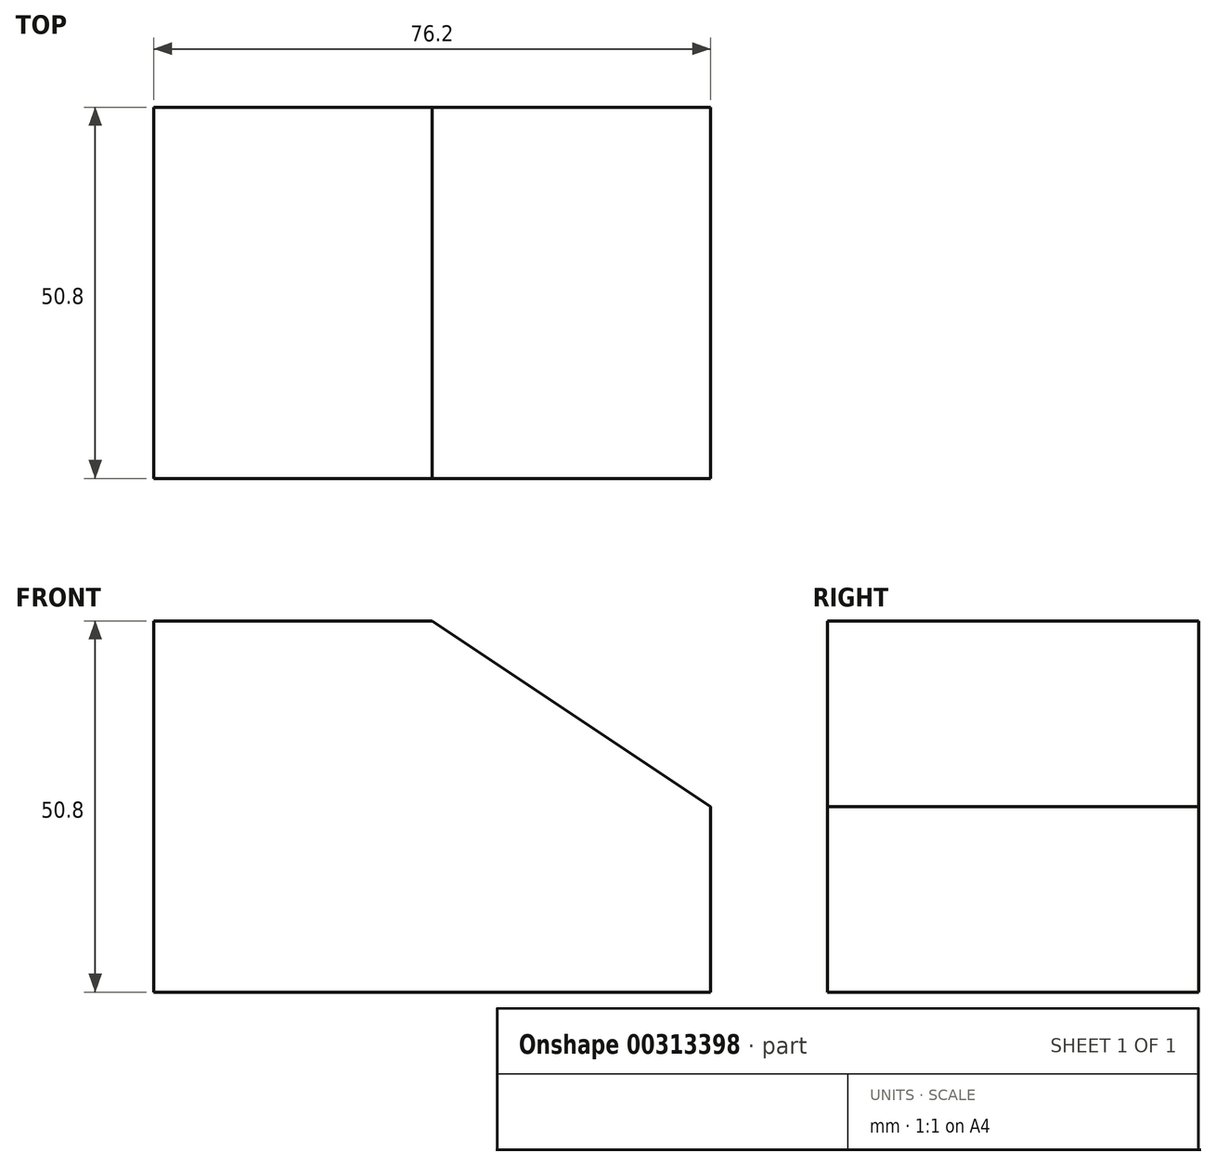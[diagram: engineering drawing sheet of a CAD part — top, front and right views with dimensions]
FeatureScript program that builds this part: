
annotation { "Feature Type Name" : "Feature", "Feature Type Description" : "" }
export const myFeature = defineFeature(function(context is Context, id is Id, definition is map)
    precondition{}
    {
        {
            var Q0;
            Q0=qCreatedBy(makeId("Front.planeOp"),FACE);
            var sketch = newSketch(context, id + "F0", { "sketchPlane" : qUnion([Q0])});
            skLineSegment(sketch, "E0", {"start": v(-31.91, -34.37) * mm, "end": v(44.29, -34.37) * mm});
            skLineSegment(sketch, "E1", {"start": v(44.29, -34.37) * mm, "end": v(44.29, -8.97) * mm});
            skLineSegment(sketch, "E2", {"start": v(44.29, -8.97) * mm, "end": v(6.19, 16.43) * mm});
            skLineSegment(sketch, "E3", {"start": v(6.19, 16.43) * mm, "end": v(-31.91, 16.43) * mm});
            skLineSegment(sketch, "E4", {"start": v(-31.91, 16.43) * mm, "end": v(-31.91, -34.37) * mm});
            skSolve(sketch);
        }
        {
            var Q0;
            Q0=makeQuery(id+"F0.imprint","IMPRINT",FACE,{"disambiguationData":[TD([[makeQuery(id+"F0.imprint","IMPRINT",EDGE,{"derivedFrom":sQuery(id+"F0.wireOp",EDGE,"E0")}),1.0]])]});
            extrude(context, id + "F1", {"entities" : qUnion([Q0]), "depth" : 50.8 * mm});
        }
    });
